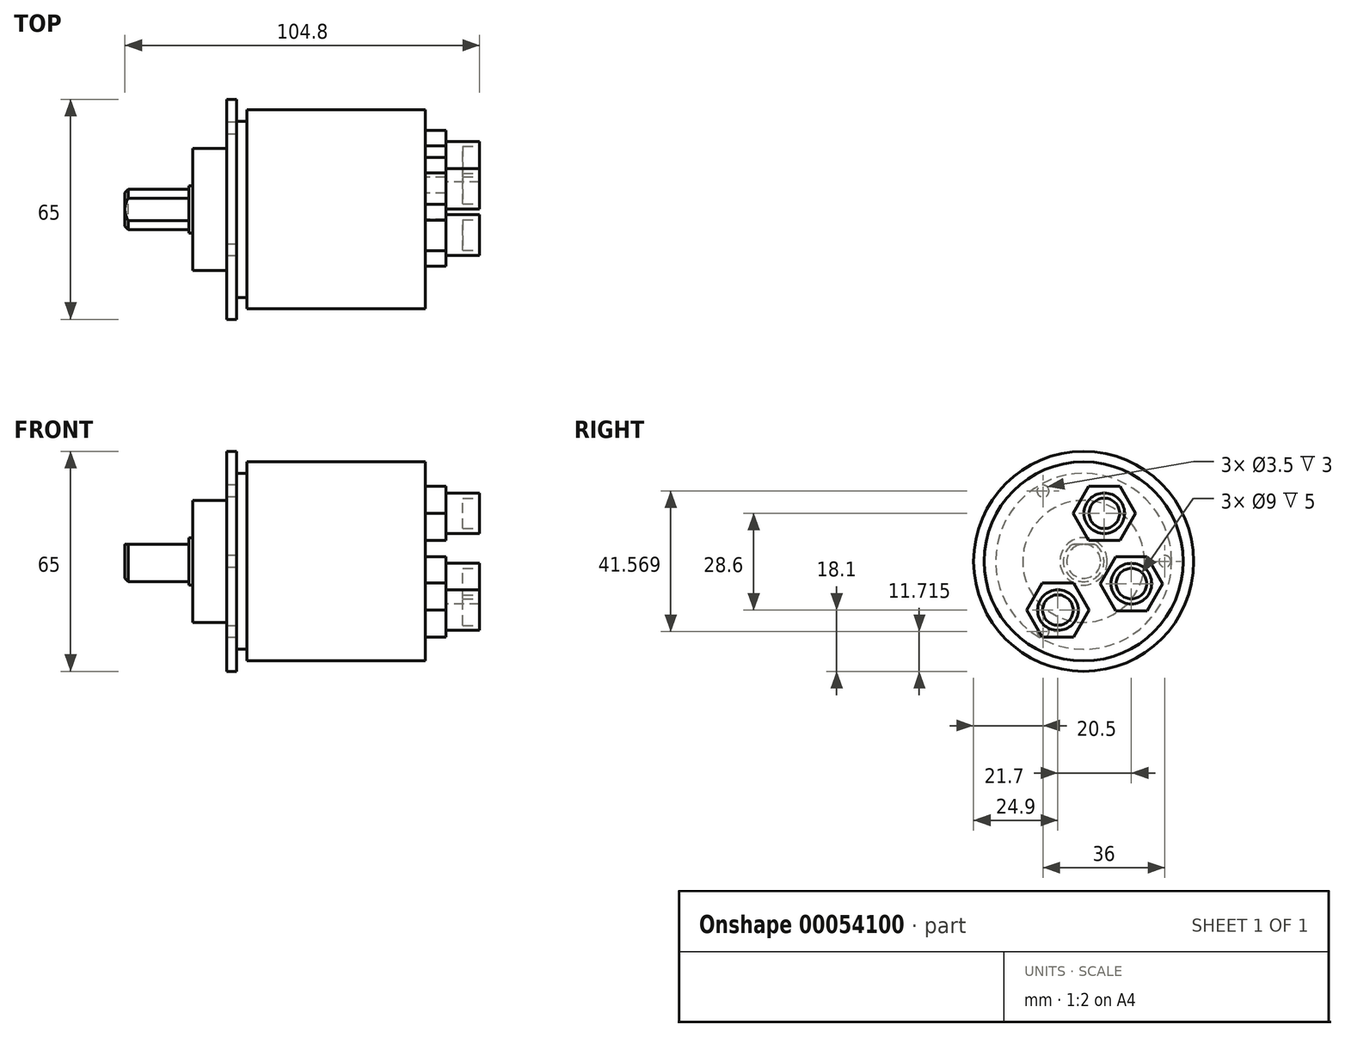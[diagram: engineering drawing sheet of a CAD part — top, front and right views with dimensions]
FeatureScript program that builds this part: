
annotation { "Feature Type Name" : "Feature", "Feature Type Description" : "" }
export const myFeature = defineFeature(function(context is Context, id is Id, definition is map)
    precondition{}
    {
        {
            var Q0;
            Q0=qCreatedBy(makeId("Right.planeOp"),FACE);
            var sketch = newSketch(context, id + "F0", { "sketchPlane" : qUnion([Q0])});
            skCircle(sketch, "E0", {"center": v(0, 0) * mm, "radius": 6 * mm});
            skSolve(sketch);
        }
        {
            var Q0;
            Q0 = qSketchRegion(id + "F0", true);
            extrude(context, id + "F1", {"entities" : qUnion([Q0]), "oppositeDirection" : true, "depth" : 18.9 * mm});
        }
        {
            var Q0;
            Q0=qCreatedBy(makeId("Right.planeOp"),FACE);
            var sketch = newSketch(context, id + "F2", { "sketchPlane" : qUnion([Q0])});
            skLineSegment(sketch, "E1", {"start": v(-18, 0) * mm, "end": v(18.18, 0) * mm, "construction": true});
            skLineSegment(sketch, "E2.0", {"start": v(-18, 5) * mm, "end": v(18.18, 5) * mm});
            skLineSegment(sketch, "E3.bottom", {"start": v(-10.5, 5) * mm, "end": v(10.66, 5) * mm});
            skLineSegment(sketch, "E3.top", {"start": v(-10.5, 9.93) * mm, "end": v(10.66, 9.93) * mm});
            skLineSegment(sketch, "E3.left", {"start": v(-10.5, 5) * mm, "end": v(-10.5, 9.93) * mm});
            skLineSegment(sketch, "E3.right", {"start": v(10.66, 5) * mm, "end": v(10.66, 9.93) * mm});
            skSolve(sketch);
        }
        {
            var Q0;
            Q0 = qSketchRegion(id + "F2", true);
            extrude(context, id + "F3", {"entities" : qUnion([Q0]), "operationType" : NewBodyOperationType.REMOVE, "endBound" : BoundingType.THROUGH_ALL, "oppositeDirection" : true, "depth" : 25 * mm});
        }
        {
            var Q0;
            Q0=makeQuery(id+"F1.opExtrude","CAP_EDGE",EDGE,{"disambiguationData":[OSD([sQuery(id+"F0.wireOp",EDGE,"E0")])],"isStart":false});
            chamfer(context, id + "F4", {"entities" : qUnion([Q0]), "width" : 1 * mm, "tangentPropagation" : true});
        }
        {
            var Q0;
            Q0=makeQuery(id+"F1.opExtrude","CAP_FACE",FACE,{"disambiguationData":[OSD([sQuery(id+"F0.wireOp",EDGE,"E0")])],"isStart":true});
            var sketch = newSketch(context, id + "F5", { "sketchPlane" : qUnion([Q0])});
            skCircle(sketch, "E4", {"center": v(0, 0) * mm, "radius": 7 * mm});
            skSolve(sketch);
        }
        {
            var Q0;
            Q0 = qSketchRegion(id + "F5", true);
            extrude(context, id + "F6", {"entities" : qUnion([Q0]), "operationType" : NewBodyOperationType.ADD, "depth" : 1.1 * mm});
        }
        {
            var Q0;
            Q0=makeQuery(id+"F6.opExtrude","CAP_FACE",FACE,{"disambiguationData":[OSD([sQuery(id+"F5.wireOp",EDGE,"E4")])],"isStart":false});
            var sketch = newSketch(context, id + "F7", { "sketchPlane" : qUnion([Q0])});
            skCircle(sketch, "E5", {"center": v(0, 0) * mm, "radius": 18 * mm});
            skSolve(sketch);
        }
        {
            var Q0;
            Q0 = qSketchRegion(id + "F7", true);
            extrude(context, id + "F8", {"entities" : qUnion([Q0]), "operationType" : NewBodyOperationType.ADD, "depth" : 10 * mm});
        }
        {
            var Q0;
            Q0=makeQuery(id+"F8.opExtrude","CAP_FACE",FACE,{"disambiguationData":[OSD([sQuery(id+"F7.wireOp",EDGE,"E5")])],"isStart":false});
            var sketch = newSketch(context, id + "F9", { "sketchPlane" : qUnion([Q0])});
            skCircle(sketch, "E6", {"center": v(0, 0) * mm, "radius": 32.5 * mm});
            skSolve(sketch);
        }
        {
            var Q0;
            Q0 = qSketchRegion(id + "F9", true);
            extrude(context, id + "F10", {"entities" : qUnion([Q0]), "operationType" : NewBodyOperationType.ADD, "depth" : 3 * mm});
        }
        {
            var Q0;
            Q0=makeQuery(id+"F10.opExtrude","CAP_FACE",FACE,{"disambiguationData":[OSD([sQuery(id+"F9.wireOp",EDGE,"E6")])],"isStart":false});
            var sketch = newSketch(context, id + "F11", { "sketchPlane" : qUnion([Q0])});
            skCircle(sketch, "E7", {"center": v(0, 0) * mm, "radius": 26 * mm});
            skSolve(sketch);
        }
        {
            var Q0;
            Q0 = qSketchRegion(id + "F11", true);
            extrude(context, id + "F12", {"entities" : qUnion([Q0]), "operationType" : NewBodyOperationType.ADD, "depth" : 3 * mm});
        }
        {
            var Q0;
            Q0=makeQuery(id+"F10.opExtrude","CAP_FACE",FACE,{"disambiguationData":[OSD([sQuery(id+"F9.wireOp",EDGE,"E6")])],"isStart":true});
            cPlane(context, id + "F13", {"entities" : qUnion([Q0]), "cplaneType" : CPlaneType.OFFSET, "offset" : 58.8 * mm, "oppositeDirection" : true, "width" : 150 * mm, "height" : 150 * mm});
        }
        {
            var Q0;
            Q0=qCreatedBy(id+"F13.planeOp",FACE);
            var sketch = newSketch(context, id + "F14", { "sketchPlane" : qUnion([Q0])});
            skCircle(sketch, "E8", {"center": v(0, 0) * mm, "radius": 29.4 * mm});
            skSolve(sketch);
        }
        {
            var Q0;
            Q0 = qSketchRegion(id + "F14", true);
            var Q1;
            Q1=makeQuery(id+"F12.opExtrude","CAP_FACE",FACE,{"disambiguationData":[OSD([sQuery(id+"F11.wireOp",EDGE,"E7")])],"isStart":false});
            extrude(context, id + "F15", {"entities" : qUnion([Q0]), "operationType" : NewBodyOperationType.ADD, "endBound" : BoundingType.UP_TO_SURFACE, "endBoundEntityFace" : qUnion([Q1]), "depth" : 25 * mm});
        }
        {
            var Q0;
            Q0=makeQuery(id+"F10.opExtrude","CAP_FACE",FACE,{"disambiguationData":[OSD([sQuery(id+"F9.wireOp",EDGE,"E6")])],"isStart":true});
            var sketch = newSketch(context, id + "F16", { "sketchPlane" : qUnion([Q0])});
            skLineSegment(sketch, "E9", {"start": v(0, 0) * mm, "end": v(-37.53, 0) * mm, "construction": true});
            skCircle(sketch, "E10", {"center": v(0, 0) * mm, "radius": 24 * mm, "construction": true});
            skPoint(sketch, "E11", {"position": v(-24, 0) * mm});
            skPoint(sketch, "E12.1.0", {"position": v(12, -20.78) * mm});
            skPoint(sketch, "E12.2.0", {"position": v(12, 20.78) * mm});
            skCircle(sketch, "E13", {"center": v(-24, 0) * mm, "radius": 1.75 * mm});
            skCircle(sketch, "E14.1.0", {"center": v(12, -20.78) * mm, "radius": 1.75 * mm});
            skCircle(sketch, "E14.2.0", {"center": v(12, 20.78) * mm, "radius": 1.75 * mm});
            skSolve(sketch);
        }
        {
            var Q0;
            Q0 = qSketchRegion(id + "F16", true);
            extrude(context, id + "F17", {"entities" : qUnion([Q0]), "operationType" : NewBodyOperationType.REMOVE, "oppositeDirection" : true, "depth" : 3 * mm});
        }
        {
            var Q0;
            Q0=makeQuery(id+"F15.opExtrude","CAP_FACE",FACE,{"disambiguationData":[OSD([sQuery(id+"F14.wireOp",EDGE,"E8")])],"isStart":true});
            var sketch = newSketch(context, id + "F18", { "sketchPlane" : qUnion([Q0])});
            skLineSegment(sketch, "E15", {"start": v(0, 47.06) * mm, "end": v(0, -42.51) * mm, "construction": true});
            skLineSegment(sketch, "E16", {"start": v(0, 0) * mm, "end": v(46.06, 0) * mm, "construction": true});
            skLineSegment(sketch, "E17", {"start": v(0, 0) * mm, "end": v(42.94, -20.02) * mm, "construction": true});
            skLineSegment(sketch, "E18.0", {"start": v(14.1, 45.36) * mm, "end": v(14.1, -42.51) * mm, "construction": true});
            skLineSegment(sketch, "E19", {"start": v(0, 0) * mm, "end": v(-39.96, 0) * mm, "construction": true});
            skLineSegment(sketch, "E20.0", {"start": v(6.1, 14.2) * mm, "end": v(-39.96, 14.2) * mm, "construction": true});
            skLineSegment(sketch, "E21.0", {"start": v(6.1, 47.06) * mm, "end": v(6.1, -42.51) * mm, "construction": true});
            skPoint(sketch, "E22", {"position": v(6.1, 14.2) * mm});
            skPoint(sketch, "E23", {"position": v(14.1, -6.57) * mm});
            skLineSegment(sketch, "E24.0", {"start": v(0, -14.4) * mm, "end": v(-39.96, -14.4) * mm, "construction": true});
            skLineSegment(sketch, "E25.0", {"start": v(-7.6, 47.06) * mm, "end": v(-7.6, -42.51) * mm, "construction": true});
            skPoint(sketch, "E26", {"position": v(-7.6, -14.4) * mm});
            skCircle(sketch, "E27.cCircle", {"center": v(14.1, -6.57) * mm, "radius": 8 * mm});
            skLineSegment(sketch, "E27.0", {"start": v(9.48, 1.43) * mm, "end": v(18.72, 1.43) * mm});
            skLineSegment(sketch, "E27.1", {"start": v(18.72, 1.43) * mm, "end": v(23.34, -6.57) * mm});
            skLineSegment(sketch, "E27.2", {"start": v(23.34, -6.57) * mm, "end": v(18.72, -14.57) * mm});
            skLineSegment(sketch, "E27.3", {"start": v(18.72, -14.57) * mm, "end": v(9.48, -14.57) * mm});
            skLineSegment(sketch, "E27.4", {"start": v(9.48, -14.57) * mm, "end": v(4.86, -6.57) * mm});
            skLineSegment(sketch, "E27.5", {"start": v(4.86, -6.57) * mm, "end": v(9.48, 1.43) * mm});
            skPoint(sketch, "E27.0.midPoint", {"position": v(14.1, 1.43) * mm});
            skCircle(sketch, "E28.cCircle", {"center": v(6.1, 14.2) * mm, "radius": 8 * mm, "construction": true});
            skLineSegment(sketch, "E28.0", {"start": v(1.48, 22.2) * mm, "end": v(10.72, 22.2) * mm});
            skLineSegment(sketch, "E28.1", {"start": v(10.72, 22.2) * mm, "end": v(15.34, 14.2) * mm});
            skLineSegment(sketch, "E28.2", {"start": v(15.34, 14.2) * mm, "end": v(10.72, 6.2) * mm});
            skLineSegment(sketch, "E28.3", {"start": v(10.72, 6.2) * mm, "end": v(1.48, 6.2) * mm});
            skLineSegment(sketch, "E28.4", {"start": v(1.48, 6.2) * mm, "end": v(-3.14, 14.2) * mm});
            skLineSegment(sketch, "E28.5", {"start": v(-3.14, 14.2) * mm, "end": v(1.48, 22.2) * mm});
            skPoint(sketch, "E28.0.midPoint", {"position": v(6.1, 22.2) * mm});
            skCircle(sketch, "E29.cCircle", {"center": v(-7.6, -14.4) * mm, "radius": 8 * mm, "construction": true});
            skLineSegment(sketch, "E29.0", {"start": v(-12.22, -6.4) * mm, "end": v(-2.98, -6.4) * mm});
            skLineSegment(sketch, "E29.1", {"start": v(-2.98, -6.4) * mm, "end": v(1.64, -14.4) * mm});
            skLineSegment(sketch, "E29.2", {"start": v(1.64, -14.4) * mm, "end": v(-2.98, -22.4) * mm});
            skLineSegment(sketch, "E29.3", {"start": v(-2.98, -22.4) * mm, "end": v(-12.22, -22.4) * mm});
            skLineSegment(sketch, "E29.4", {"start": v(-12.22, -22.4) * mm, "end": v(-16.84, -14.4) * mm});
            skLineSegment(sketch, "E29.5", {"start": v(-16.84, -14.4) * mm, "end": v(-12.22, -6.4) * mm});
            skPoint(sketch, "E29.0.midPoint", {"position": v(-7.6, -6.4) * mm});
            skSolve(sketch);
        }
        {
            var Q0;
            Q0 = qSketchRegion(id + "F18", true);
            extrude(context, id + "F19", {"entities" : qUnion([Q0]), "operationType" : NewBodyOperationType.ADD, "depth" : 6 * mm});
        }
        {
            var Q0;
            Q0=makeQuery(id+"F19.opExtrude","CAP_FACE",FACE,{"disambiguationData":[OSD([sQuery(id+"F18.wireOp",EDGE,"E28.0"),sQuery(id+"F18.wireOp",EDGE,"E28.1"),sQuery(id+"F18.wireOp",EDGE,"E28.2"),sQuery(id+"F18.wireOp",EDGE,"E28.3"),sQuery(id+"F18.wireOp",EDGE,"E28.4"),sQuery(id+"F18.wireOp",EDGE,"E28.5")])],"isStart":false});
            var sketch = newSketch(context, id + "F20", { "sketchPlane" : qUnion([Q0])});
            skPoint(sketch, "E30.0", {"position": v(6.1, 14.2) * mm});
            skPoint(sketch, "E31.0", {"position": v(14.1, -6.57) * mm});
            skPoint(sketch, "E32.0", {"position": v(-7.6, -14.4) * mm});
            skCircle(sketch, "E33", {"center": v(6.1, 14.2) * mm, "radius": 6 * mm});
            skCircle(sketch, "E34", {"center": v(14.1, -6.57) * mm, "radius": 6 * mm});
            skCircle(sketch, "E35", {"center": v(-7.6, -14.4) * mm, "radius": 6 * mm});
            skSolve(sketch);
        }
        {
            var Q0;
            Q0 = qSketchRegion(id + "F20", true);
            extrude(context, id + "F21", {"entities" : qUnion([Q0]), "operationType" : NewBodyOperationType.ADD, "depth" : 10 * mm});
        }
        {
            var Q0;
            Q0=makeQuery(id+"F21.opExtrude","CAP_FACE",FACE,{"disambiguationData":[OSD([sQuery(id+"F20.wireOp",EDGE,"E33")])],"isStart":false});
            var sketch = newSketch(context, id + "F22", { "sketchPlane" : qUnion([Q0])});
            skCircle(sketch, "E36.0", {"center": v(6.1, 14.2) * mm, "radius": 6 * mm, "construction": true});
            skCircle(sketch, "E37.0", {"center": v(14.1, -6.57) * mm, "radius": 6 * mm, "construction": true});
            skCircle(sketch, "E38.0", {"center": v(-7.6, -14.4) * mm, "radius": 6 * mm, "construction": true});
            skCircle(sketch, "E39.0", {"center": v(6.1, 14.2) * mm, "radius": 4.5 * mm});
            skCircle(sketch, "E40", {"center": v(-7.6, -14.4) * mm, "radius": 4.5 * mm});
            skCircle(sketch, "E41", {"center": v(14.1, -6.57) * mm, "radius": 4.5 * mm});
            skSolve(sketch);
        }
        {
            var Q0;
            Q0 = qSketchRegion(id + "F22", true);
            extrude(context, id + "F23", {"entities" : qUnion([Q0]), "operationType" : NewBodyOperationType.REMOVE, "oppositeDirection" : true, "depth" : 5 * mm});
        }
    });
